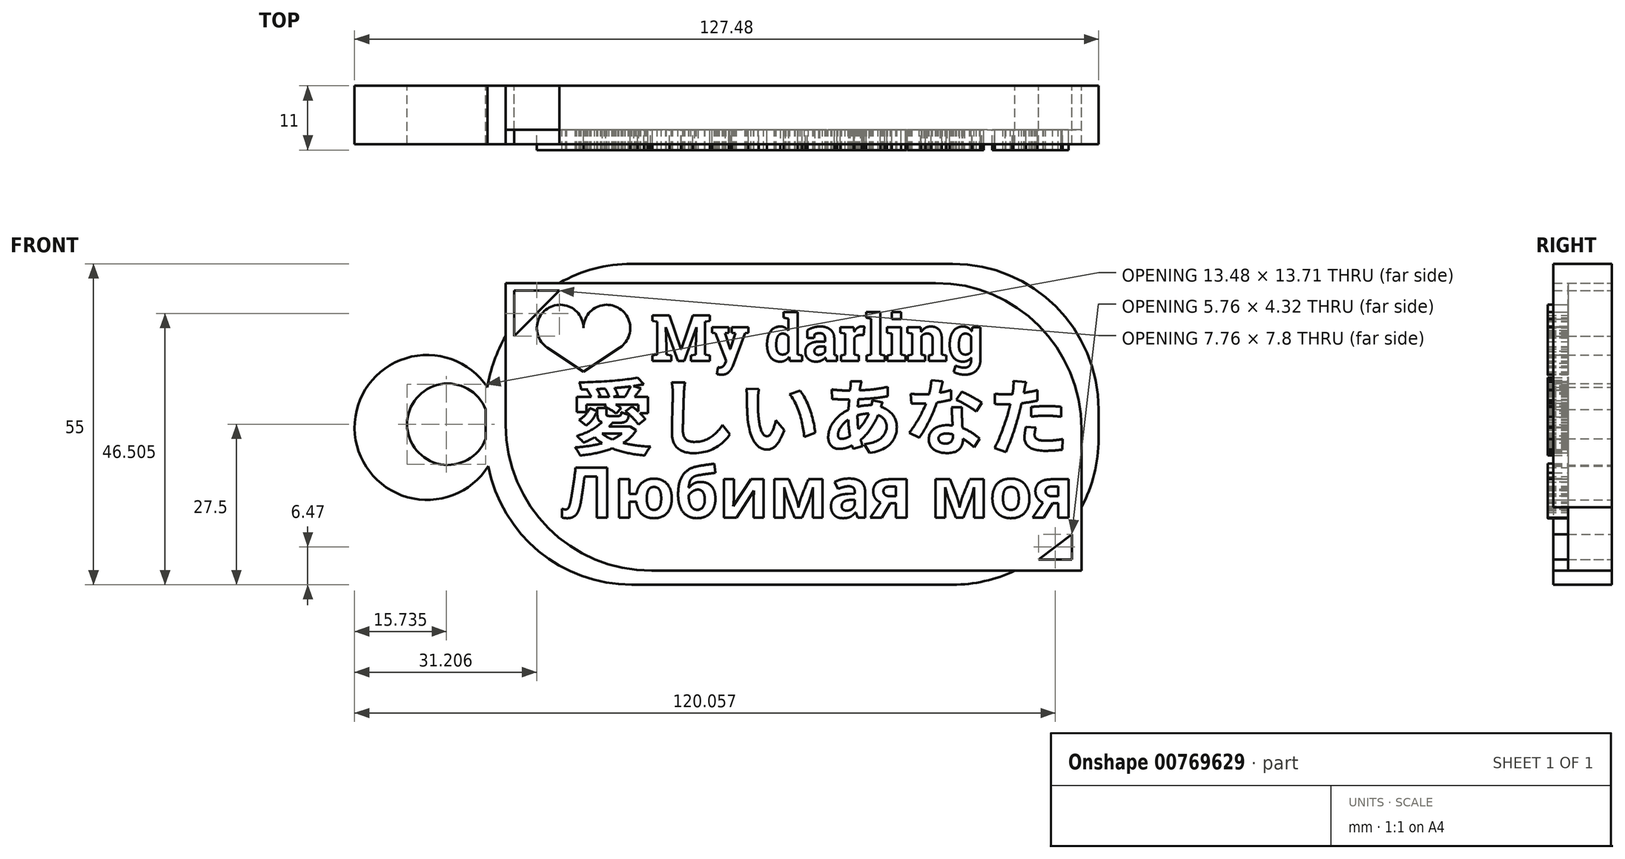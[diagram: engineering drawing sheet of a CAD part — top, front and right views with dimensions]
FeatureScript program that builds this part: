
annotation { "Feature Type Name" : "Feature", "Feature Type Description" : "" }
export const myFeature = defineFeature(function(context is Context, id is Id, definition is map)
    precondition{}
    {
        {
            var Q0;
            Q0=qCreatedBy(makeId("Front.planeOp"),FACE);
            var sketch = newSketch(context, id + "F0", { "sketchPlane" : qUnion([Q0])});
            skLineSegment(sketch, "E0.bottom", {"start": v(4.18, 28.74) * mm, "end": v(59.18, 28.74) * mm});
            skLineSegment(sketch, "E0.top", {"start": v(4.18, -26.26) * mm, "end": v(59.18, -26.26) * mm});
            skLineSegment(sketch, "E0.left", {"start": v(-20.82, 3.74) * mm, "end": v(-20.82, -1.26) * mm});
            skLineSegment(sketch, "E0.right", {"start": v(84.18, 3.74) * mm, "end": v(84.18, -1.26) * mm});
            skPoint(sketch, "E1.visualSharp", {"position": v(84.18, 28.74) * mm});
            skArc(sketch, "E1.filletArc", {"start": v(84.18, 3.74) * mm, "mid": v(76.85, 21.42) * mm, "end": v(59.18, 28.74) * mm});
            skPoint(sketch, "E2.visualSharp", {"position": v(84.18, -26.26) * mm});
            skArc(sketch, "E2.filletArc", {"start": v(59.18, -26.26) * mm, "mid": v(64.63, -25.66) * mm, "end": v(69.82, -23.88) * mm});
            skPoint(sketch, "E3.visualSharp", {"position": v(-20.82, -26.26) * mm});
            skArc(sketch, "E3.filletArc", {"start": v(-20.38, -5.94) * mm, "mid": v(-11.76, -20.52) * mm, "end": v(4.18, -26.26) * mm});
            skPoint(sketch, "E4.visualSharp", {"position": v(-20.82, 28.74) * mm});
            skArc(sketch, "E4.filletArc", {"start": v(4.18, 28.74) * mm, "mid": v(-2.23, 27.9) * mm, "end": v(-8.22, 25.45) * mm});
            skLineSegment(sketch, "E5.bottom", {"start": v(-17.41, 25.45) * mm, "end": v(56.26, 25.45) * mm});
            skLineSegment(sketch, "E5.top", {"start": v(7.59, -23.88) * mm, "end": v(81.26, -23.88) * mm});
            skLineSegment(sketch, "E5.left", {"start": v(-17.41, 25.45) * mm, "end": v(-17.41, 1.12) * mm});
            skLineSegment(sketch, "E5.right", {"start": v(81.26, 0.45) * mm, "end": v(81.26, -23.88) * mm});
            skPoint(sketch, "E6.visualSharp", {"position": v(-17.41, -23.88) * mm});
            skArc(sketch, "E6.filletArc", {"start": v(-17.41, 1.12) * mm, "mid": v(-10.09, -16.56) * mm, "end": v(7.59, -23.88) * mm});
            skPoint(sketch, "E7.visualSharp", {"position": v(81.26, 25.45) * mm});
            skArc(sketch, "E7.filletArc", {"start": v(81.26, 0.45) * mm, "mid": v(73.94, 18.13) * mm, "end": v(56.26, 25.45) * mm});
            skArc(sketch, "E8", {"start": v(-20.82, 3.74) * mm, "mid": v(-34.3, 1.24) * mm, "end": v(-20.82, -1.26) * mm});
            skArc(sketch, "E9", {"start": v(-20.53, 7.55) * mm, "mid": v(-43.3, 0.55) * mm, "end": v(-20.38, -5.94) * mm});
            skArc(sketch, "E10.trimOffspring", {"start": v(-17.41, 16.35) * mm, "mid": v(-19.38, 12.1) * mm, "end": v(-20.53, 7.55) * mm});
            skArc(sketch, "E11.trimOffspring", {"start": v(81.26, -12.98) * mm, "mid": v(83.44, -7.3) * mm, "end": v(84.18, -1.26) * mm});
            skPoint(sketch, "E12.center.orphan", {"position": v(-8.07, 15.63) * mm});
            skPoint(sketch, "E13.center.orphan", {"position": v(7.45, 15.63) * mm});
            skPoint(sketch, "E14.end.orphan", {"position": v(-0.31, 15.63) * mm});
            skCircle(sketch, "E15", {"center": v(-8.07, 17.71) * mm, "radius": 4 * mm});
            skCircle(sketch, "E16", {"center": v(-0.07, 17.71) * mm, "radius": 4 * mm});
            skLineSegment(sketch, "E17", {"start": v(-4.07, 10.25) * mm, "end": v(-10.29, 14.38) * mm});
            skLineSegment(sketch, "E18", {"start": v(-4.07, 10.25) * mm, "end": v(2.14, 14.38) * mm});
            skPoint(sketch, "E19.start.orphan", {"position": v(-4.07, 17.71) * mm});
            skText(sketch, "E20", { "text": "Любимая моя", "fontName": "OpenSans-Bold.ttf"});
            skText(sketch, "E21", { "text": "愛しいあなた", "fontName": "NotoSansCJKjp-Bold.otf"});
            skText(sketch, "E22", { "text": "My darling", "fontName": "RobotoSlab-Bold.ttf"});
            skLineSegment(sketch, "E23", {"start": v(-15.97, 24.14) * mm, "end": v(-15.97, 16.35) * mm});
            skLineSegment(sketch, "E24", {"start": v(-15.97, 16.35) * mm, "end": v(-8.22, 24.14) * mm});
            skLineSegment(sketch, "E25", {"start": v(-8.22, 24.14) * mm, "end": v(-15.97, 24.14) * mm});
            skLineSegment(sketch, "E26", {"start": v(73.88, -21.95) * mm, "end": v(79.64, -21.95) * mm});
            skLineSegment(sketch, "E27", {"start": v(79.64, -21.95) * mm, "end": v(79.64, -17.63) * mm});
            skLineSegment(sketch, "E28", {"start": v(79.64, -17.63) * mm, "end": v(73.88, -21.95) * mm});
            const initialGuessF0  = {"E20": [-0.00787, -0.01475, 1, 0, 0.00864], "E21": [-0.00625, -0.00286, 1, 0, 0.01026], "E22": [0.00745, 0.01208, 1, 0, 0.00792]};
            skSetInitialGuess(sketch, initialGuessF0);
            skSolve(sketch);
        }
        {
            var Q0;
            Q0=makeQuery(id+"F0.imprint","IMPRINT",FACE,{"disambiguationData":[TD([[makeQuery(id+"F0.imprint","IMPRINT",EDGE,{"derivedFrom":sQuery(id+"F0.wireOp",EDGE,"E23")}),1.0]])]});
            var Q1;
            Q1=makeQuery(id+"F0.imprint","IMPRINT",FACE,{"disambiguationData":[TD([[makeQuery(id+"F0.imprint","IMPRINT",EDGE,{"derivedFrom":sQuery(id+"F0.wireOp",EDGE,"E0.bottom")}),-1.0]])]});
            var Q2;
            Q2=makeQuery(id+"F0.imprint","IMPRINT",FACE,{"disambiguationData":[TD([[makeQuery(id+"F0.imprint","IMPRINT",EDGE,{"derivedFrom":sQuery(id+"F0.wireOp",EDGE,"E26")}),1.0]])]});
            var Q3;
            Q3=makeQuery(id+"F0.imprint","IMPRINT",FACE,{"disambiguationData":[TD([[makeQuery(id+"F0.imprint","IMPRINT",EDGE,{"derivedFrom":sQuery(id+"F0.wireOp",EDGE,"E0.top")}),1.0]])]});
            extrude(context, id + "F1", {"entities" : qUnion([Q0, Q1, Q2, Q3]), "depth" : 10 * mm, "offsetDistance" : 25 * mm});
        }
        {
            var Q0;
            {var subQ9=sQuery(id+"F0.wireOp",EDGE,"E6.filletArc");Q0=makeQuery(id+"F0.imprint","IMPRINT",FACE,{"disambiguationData":[TD([[makeQuery(id+"F0.imprint","IMPRINT",EDGE,{"derivedFrom":subQ9}),1.0]])]});}
            extrude(context, id + "F2", {"entities" : qUnion([Q0]), "depth" : 7.5 * mm, "offsetDistance" : 25 * mm});
        }
        {
            var Q0;
            {var subQ0=sQuery(id+"F0.wireOp",EDGE,"E16");var subQ1=makeQuery(id+"F0.imprint","INTERSECT",VERTEX,{"derivedFrom":[subQ0,sQuery(id+"F0.wireOp",EDGE,"E18")]});Q0=makeQuery(id+"F0.imprint","IMPRINT",FACE,{"disambiguationData":[TD([[makeQuery(id+"F0.imprint","IMPRINT",EDGE,{"disambiguationData":[TD([[subQ1,1.0]])],"derivedFrom":subQ0}),1.0]])]});}
            var Q1;
            {var subQ0=sQuery(id+"F0.wireOp",EDGE,"E15");var subQ1=makeQuery(id+"F0.imprint","INTERSECT",VERTEX,{"derivedFrom":[subQ0,sQuery(id+"F0.wireOp",EDGE,"E17")]});Q1=makeQuery(id+"F0.imprint","IMPRINT",FACE,{"disambiguationData":[TD([[makeQuery(id+"F0.imprint","IMPRINT",EDGE,{"disambiguationData":[TD([[subQ1,1.0]])],"derivedFrom":subQ0}),1.0]])]});}
            var Q2;
            {var subQ0=sQuery(id+"F0.wireOp",EDGE,"E17");Q2=makeQuery(id+"F0.imprint","IMPRINT",FACE,{"disambiguationData":[TD([[makeQuery(id+"F0.imprint","IMPRINT",EDGE,{"derivedFrom":subQ0}),-1.0]])]});}
            var Q3;
            Q3=makeQuery(id+"F0.imprint","IMPRINT",FACE,{"disambiguationData":[TD([[makeQuery(id+"F0.imprint","IMPRINT",EDGE,{"derivedFrom":sQuery(id+"F0.wireOp",EDGE,"E22.sketch_text.stroke-0")}),-1.0]])]});
            var Q4;
            Q4=makeQuery(id+"F0.imprint","IMPRINT",FACE,{"disambiguationData":[TD([[makeQuery(id+"F0.imprint","IMPRINT",EDGE,{"derivedFrom":sQuery(id+"F0.wireOp",EDGE,"E22.sketch_text.stroke-31")}),-1.0]])]});
            var Q5;
            Q5=makeQuery(id+"F0.imprint","IMPRINT",FACE,{"disambiguationData":[TD([[makeQuery(id+"F0.imprint","IMPRINT",EDGE,{"derivedFrom":sQuery(id+"F0.wireOp",EDGE,"E22.sketch_text.stroke-57")}),-1.0]])]});
            var Q6;
            Q6=makeQuery(id+"F0.imprint","IMPRINT",FACE,{"disambiguationData":[TD([[makeQuery(id+"F0.imprint","IMPRINT",EDGE,{"derivedFrom":sQuery(id+"F0.wireOp",EDGE,"E22.sketch_text.stroke-86")}),-1.0]])]});
            var Q7;
            Q7=makeQuery(id+"F0.imprint","IMPRINT",FACE,{"disambiguationData":[TD([[makeQuery(id+"F0.imprint","IMPRINT",EDGE,{"derivedFrom":sQuery(id+"F0.wireOp",EDGE,"E22.sketch_text.stroke-121")}),-1.0]])]});
            var Q8;
            Q8=makeQuery(id+"F0.imprint","IMPRINT",FACE,{"disambiguationData":[TD([[makeQuery(id+"F0.imprint","IMPRINT",EDGE,{"derivedFrom":sQuery(id+"F0.wireOp",EDGE,"E22.sketch_text.stroke-140")}),-1.0]])]});
            var Q9;
            Q9=makeQuery(id+"F0.imprint","IMPRINT",FACE,{"disambiguationData":[TD([[makeQuery(id+"F0.imprint","IMPRINT",EDGE,{"derivedFrom":sQuery(id+"F0.wireOp",EDGE,"E22.sketch_text.stroke-150")}),-1.0]])]});
            var Q10;
            Q10=makeQuery(id+"F0.imprint","IMPRINT",FACE,{"disambiguationData":[TD([[makeQuery(id+"F0.imprint","IMPRINT",EDGE,{"derivedFrom":sQuery(id+"F0.wireOp",EDGE,"E22.sketch_text.stroke-160")}),-1.0]])]});
            var Q11;
            Q11=makeQuery(id+"F0.imprint","IMPRINT",FACE,{"disambiguationData":[TD([[makeQuery(id+"F0.imprint","IMPRINT",EDGE,{"derivedFrom":sQuery(id+"F0.wireOp",EDGE,"E22.sketch_text.stroke-164")}),-1.0]])]});
            var Q12;
            Q12=makeQuery(id+"F0.imprint","IMPRINT",FACE,{"disambiguationData":[TD([[makeQuery(id+"F0.imprint","IMPRINT",EDGE,{"derivedFrom":sQuery(id+"F0.wireOp",EDGE,"E22.sketch_text.stroke-190")}),-1.0]])]});
            var Q13;
            Q13=makeQuery(id+"F0.imprint","IMPRINT",FACE,{"disambiguationData":[TD([[makeQuery(id+"F0.imprint","IMPRINT",EDGE,{"derivedFrom":sQuery(id+"F0.wireOp",EDGE,"E21.sketch_text.stroke-0")}),1.0]])]});
            var Q14;
            Q14=makeQuery(id+"F0.imprint","IMPRINT",FACE,{"disambiguationData":[TD([[makeQuery(id+"F0.imprint","IMPRINT",EDGE,{"derivedFrom":sQuery(id+"F0.wireOp",EDGE,"E21.sketch_text.stroke-42")}),1.0]])]});
            var Q15;
            Q15=makeQuery(id+"F0.imprint","IMPRINT",FACE,{"disambiguationData":[TD([[makeQuery(id+"F0.imprint","IMPRINT",EDGE,{"derivedFrom":sQuery(id+"F0.wireOp",EDGE,"E21.sketch_text.stroke-38")}),1.0]])]});
            var Q16;
            Q16=makeQuery(id+"F0.imprint","IMPRINT",FACE,{"disambiguationData":[TD([[makeQuery(id+"F0.imprint","IMPRINT",EDGE,{"derivedFrom":sQuery(id+"F0.wireOp",EDGE,"E21.sketch_text.stroke-71")}),1.0]])]});
            var Q17;
            Q17=makeQuery(id+"F0.imprint","IMPRINT",FACE,{"disambiguationData":[TD([[makeQuery(id+"F0.imprint","IMPRINT",EDGE,{"derivedFrom":sQuery(id+"F0.wireOp",EDGE,"E21.sketch_text.stroke-81")}),1.0]])]});
            var Q18;
            Q18=makeQuery(id+"F0.imprint","IMPRINT",FACE,{"disambiguationData":[TD([[makeQuery(id+"F0.imprint","IMPRINT",EDGE,{"derivedFrom":sQuery(id+"F0.wireOp",EDGE,"E21.sketch_text.stroke-91")}),1.0]])]});
            var Q19;
            Q19=makeQuery(id+"F0.imprint","IMPRINT",FACE,{"disambiguationData":[TD([[makeQuery(id+"F0.imprint","IMPRINT",EDGE,{"derivedFrom":sQuery(id+"F0.wireOp",EDGE,"E21.sketch_text.stroke-95")}),1.0]])]});
            var Q20;
            Q20=makeQuery(id+"F0.imprint","IMPRINT",FACE,{"disambiguationData":[TD([[makeQuery(id+"F0.imprint","IMPRINT",EDGE,{"derivedFrom":sQuery(id+"F0.wireOp",EDGE,"E21.sketch_text.stroke-139")}),1.0]])]});
            var Q21;
            Q21=makeQuery(id+"F0.imprint","IMPRINT",FACE,{"disambiguationData":[TD([[makeQuery(id+"F0.imprint","IMPRINT",EDGE,{"derivedFrom":sQuery(id+"F0.wireOp",EDGE,"E21.sketch_text.stroke-135")}),1.0]])]});
            var Q22;
            Q22=makeQuery(id+"F0.imprint","IMPRINT",FACE,{"disambiguationData":[TD([[makeQuery(id+"F0.imprint","IMPRINT",EDGE,{"derivedFrom":sQuery(id+"F0.wireOp",EDGE,"E21.sketch_text.stroke-176")}),1.0]])]});
            var Q23;
            Q23=makeQuery(id+"F0.imprint","IMPRINT",FACE,{"disambiguationData":[TD([[makeQuery(id+"F0.imprint","IMPRINT",EDGE,{"derivedFrom":sQuery(id+"F0.wireOp",EDGE,"E21.sketch_text.stroke-153")}),1.0]])]});
            var Q24;
            Q24=makeQuery(id+"F0.imprint","IMPRINT",FACE,{"disambiguationData":[TD([[makeQuery(id+"F0.imprint","IMPRINT",EDGE,{"derivedFrom":sQuery(id+"F0.wireOp",EDGE,"E21.sketch_text.stroke-194")}),1.0]])]});
            var Q25;
            Q25=makeQuery(id+"F0.imprint","IMPRINT",FACE,{"disambiguationData":[TD([[makeQuery(id+"F0.imprint","IMPRINT",EDGE,{"derivedFrom":sQuery(id+"F0.wireOp",EDGE,"E21.sketch_text.stroke-170")}),1.0]])]});
            var Q26;
            Q26=makeQuery(id+"F0.imprint","IMPRINT",FACE,{"disambiguationData":[TD([[makeQuery(id+"F0.imprint","IMPRINT",EDGE,{"derivedFrom":sQuery(id+"F0.wireOp",EDGE,"E20.sketch_text.stroke-0")}),-1.0]])]});
            var Q27;
            Q27=makeQuery(id+"F0.imprint","IMPRINT",FACE,{"disambiguationData":[TD([[makeQuery(id+"F0.imprint","IMPRINT",EDGE,{"derivedFrom":sQuery(id+"F0.wireOp",EDGE,"E20.sketch_text.stroke-16")}),-1.0]])]});
            var Q28;
            Q28=makeQuery(id+"F0.imprint","IMPRINT",FACE,{"disambiguationData":[TD([[makeQuery(id+"F0.imprint","IMPRINT",EDGE,{"derivedFrom":sQuery(id+"F0.wireOp",EDGE,"E20.sketch_text.stroke-39")}),-1.0]])]});
            var Q29;
            Q29=makeQuery(id+"F0.imprint","IMPRINT",FACE,{"disambiguationData":[TD([[makeQuery(id+"F0.imprint","IMPRINT",EDGE,{"derivedFrom":sQuery(id+"F0.wireOp",EDGE,"E20.sketch_text.stroke-63")}),-1.0]])]});
            var Q30;
            Q30=makeQuery(id+"F0.imprint","IMPRINT",FACE,{"disambiguationData":[TD([[makeQuery(id+"F0.imprint","IMPRINT",EDGE,{"derivedFrom":sQuery(id+"F0.wireOp",EDGE,"E20.sketch_text.stroke-75")}),-1.0]])]});
            var Q31;
            Q31=makeQuery(id+"F0.imprint","IMPRINT",FACE,{"disambiguationData":[TD([[makeQuery(id+"F0.imprint","IMPRINT",EDGE,{"derivedFrom":sQuery(id+"F0.wireOp",EDGE,"E20.sketch_text.stroke-96")}),-1.0]])]});
            var Q32;
            Q32=makeQuery(id+"F0.imprint","IMPRINT",FACE,{"disambiguationData":[TD([[makeQuery(id+"F0.imprint","IMPRINT",EDGE,{"derivedFrom":sQuery(id+"F0.wireOp",EDGE,"E20.sketch_text.stroke-121")}),-1.0]])]});
            var Q33;
            Q33=makeQuery(id+"F0.imprint","IMPRINT",FACE,{"disambiguationData":[TD([[makeQuery(id+"F0.imprint","IMPRINT",EDGE,{"derivedFrom":sQuery(id+"F0.wireOp",EDGE,"E20.sketch_text.stroke-140")}),-1.0]])]});
            var Q34;
            Q34=makeQuery(id+"F0.imprint","IMPRINT",FACE,{"disambiguationData":[TD([[makeQuery(id+"F0.imprint","IMPRINT",EDGE,{"derivedFrom":sQuery(id+"F0.wireOp",EDGE,"E20.sketch_text.stroke-161")}),-1.0]])]});
            var Q35;
            Q35=makeQuery(id+"F0.imprint","IMPRINT",FACE,{"disambiguationData":[TD([[makeQuery(id+"F0.imprint","IMPRINT",EDGE,{"derivedFrom":sQuery(id+"F0.wireOp",EDGE,"E20.sketch_text.stroke-179")}),-1.0]])]});
            extrude(context, id + "F3", {"entities" : qUnion([Q0, Q1, Q2, Q3, Q4, Q5, Q6, Q7, Q8, Q9, Q10, Q11, Q12, Q13, Q14, Q15, Q16, Q17, Q18, Q19, Q20, Q21, Q22, Q23, Q24, Q25, Q26, Q27, Q28, Q29, Q30, Q31, Q32, Q33, Q34, Q35]), "operationType" : NewBodyOperationType.ADD, "depth" : 11 * mm, "offsetDistance" : 25 * mm});
        }
        {
            var Q0;
            Q0=makeQuery(id+"F0.imprint","IMPRINT",FACE,{"disambiguationData":[TD([[makeQuery(id+"F0.imprint","IMPRINT",EDGE,{"derivedFrom":sQuery(id+"F0.wireOp",EDGE,"E22.sketch_text.stroke-76")}),1.0]])]});
            var Q1;
            Q1=makeQuery(id+"F0.imprint","IMPRINT",FACE,{"disambiguationData":[TD([[makeQuery(id+"F0.imprint","IMPRINT",EDGE,{"derivedFrom":sQuery(id+"F0.wireOp",EDGE,"E22.sketch_text.stroke-113")}),1.0]])]});
            var Q2;
            Q2=makeQuery(id+"F0.imprint","IMPRINT",FACE,{"disambiguationData":[TD([[makeQuery(id+"F0.imprint","IMPRINT",EDGE,{"derivedFrom":sQuery(id+"F0.wireOp",EDGE,"E22.sketch_text.stroke-212")}),1.0]])]});
            var Q3;
            Q3=makeQuery(id+"F0.imprint","IMPRINT",FACE,{"disambiguationData":[TD([[makeQuery(id+"F0.imprint","IMPRINT",EDGE,{"derivedFrom":sQuery(id+"F0.wireOp",EDGE,"E21.sketch_text.stroke-153")}),-1.0]])]});
            var Q4;
            Q4=makeQuery(id+"F0.imprint","IMPRINT",FACE,{"disambiguationData":[TD([[makeQuery(id+"F0.imprint","IMPRINT",EDGE,{"derivedFrom":sQuery(id+"F0.wireOp",EDGE,"E21.sketch_text.stroke-99")}),-1.0]])]});
            var Q5;
            Q5=makeQuery(id+"F0.imprint","IMPRINT",FACE,{"disambiguationData":[TD([[makeQuery(id+"F0.imprint","IMPRINT",EDGE,{"derivedFrom":sQuery(id+"F0.wireOp",EDGE,"E21.sketch_text.stroke-95")}),-1.0]])]});
            var Q6;
            Q6=makeQuery(id+"F0.imprint","IMPRINT",FACE,{"disambiguationData":[TD([[makeQuery(id+"F0.imprint","IMPRINT",EDGE,{"derivedFrom":sQuery(id+"F0.wireOp",EDGE,"E21.sketch_text.stroke-42")}),-1.0]])]});
            var Q7;
            Q7=makeQuery(id+"F0.imprint","IMPRINT",FACE,{"disambiguationData":[TD([[makeQuery(id+"F0.imprint","IMPRINT",EDGE,{"derivedFrom":sQuery(id+"F0.wireOp",EDGE,"E21.sketch_text.stroke-0")}),-1.0]])]});
            var Q8;
            Q8=makeQuery(id+"F0.imprint","IMPRINT",FACE,{"disambiguationData":[TD([[makeQuery(id+"F0.imprint","IMPRINT",EDGE,{"derivedFrom":sQuery(id+"F0.wireOp",EDGE,"E21.sketch_text.stroke-5")}),-1.0]])]});
            var Q9;
            Q9=makeQuery(id+"F0.imprint","IMPRINT",FACE,{"disambiguationData":[TD([[makeQuery(id+"F0.imprint","IMPRINT",EDGE,{"derivedFrom":sQuery(id+"F0.wireOp",EDGE,"E20.sketch_text.stroke-31")}),1.0]])]});
            var Q10;
            Q10=makeQuery(id+"F0.imprint","IMPRINT",FACE,{"disambiguationData":[TD([[makeQuery(id+"F0.imprint","IMPRINT",EDGE,{"derivedFrom":sQuery(id+"F0.wireOp",EDGE,"E20.sketch_text.stroke-56")}),1.0]])]});
            var Q11;
            Q11=makeQuery(id+"F0.imprint","IMPRINT",FACE,{"disambiguationData":[TD([[makeQuery(id+"F0.imprint","IMPRINT",EDGE,{"derivedFrom":sQuery(id+"F0.wireOp",EDGE,"E20.sketch_text.stroke-114")}),1.0]])]});
            var Q12;
            Q12=makeQuery(id+"F0.imprint","IMPRINT",FACE,{"disambiguationData":[TD([[makeQuery(id+"F0.imprint","IMPRINT",EDGE,{"derivedFrom":sQuery(id+"F0.wireOp",EDGE,"E20.sketch_text.stroke-133")}),1.0]])]});
            var Q13;
            Q13=makeQuery(id+"F0.imprint","IMPRINT",FACE,{"disambiguationData":[TD([[makeQuery(id+"F0.imprint","IMPRINT",EDGE,{"derivedFrom":sQuery(id+"F0.wireOp",EDGE,"E20.sketch_text.stroke-161")}),1.0]])]});
            var Q14;
            Q14=makeQuery(id+"F0.imprint","IMPRINT",FACE,{"disambiguationData":[TD([[makeQuery(id+"F0.imprint","IMPRINT",EDGE,{"derivedFrom":sQuery(id+"F0.wireOp",EDGE,"E20.sketch_text.stroke-191")}),1.0]])]});
            extrude(context, id + "F4", {"entities" : qUnion([Q0, Q1, Q2, Q3, Q4, Q5, Q6, Q7, Q8, Q9, Q10, Q11, Q12, Q13, Q14]), "operationType" : NewBodyOperationType.ADD, "depth" : 7.5 * mm, "offsetDistance" : 25 * mm});
        }
    });
